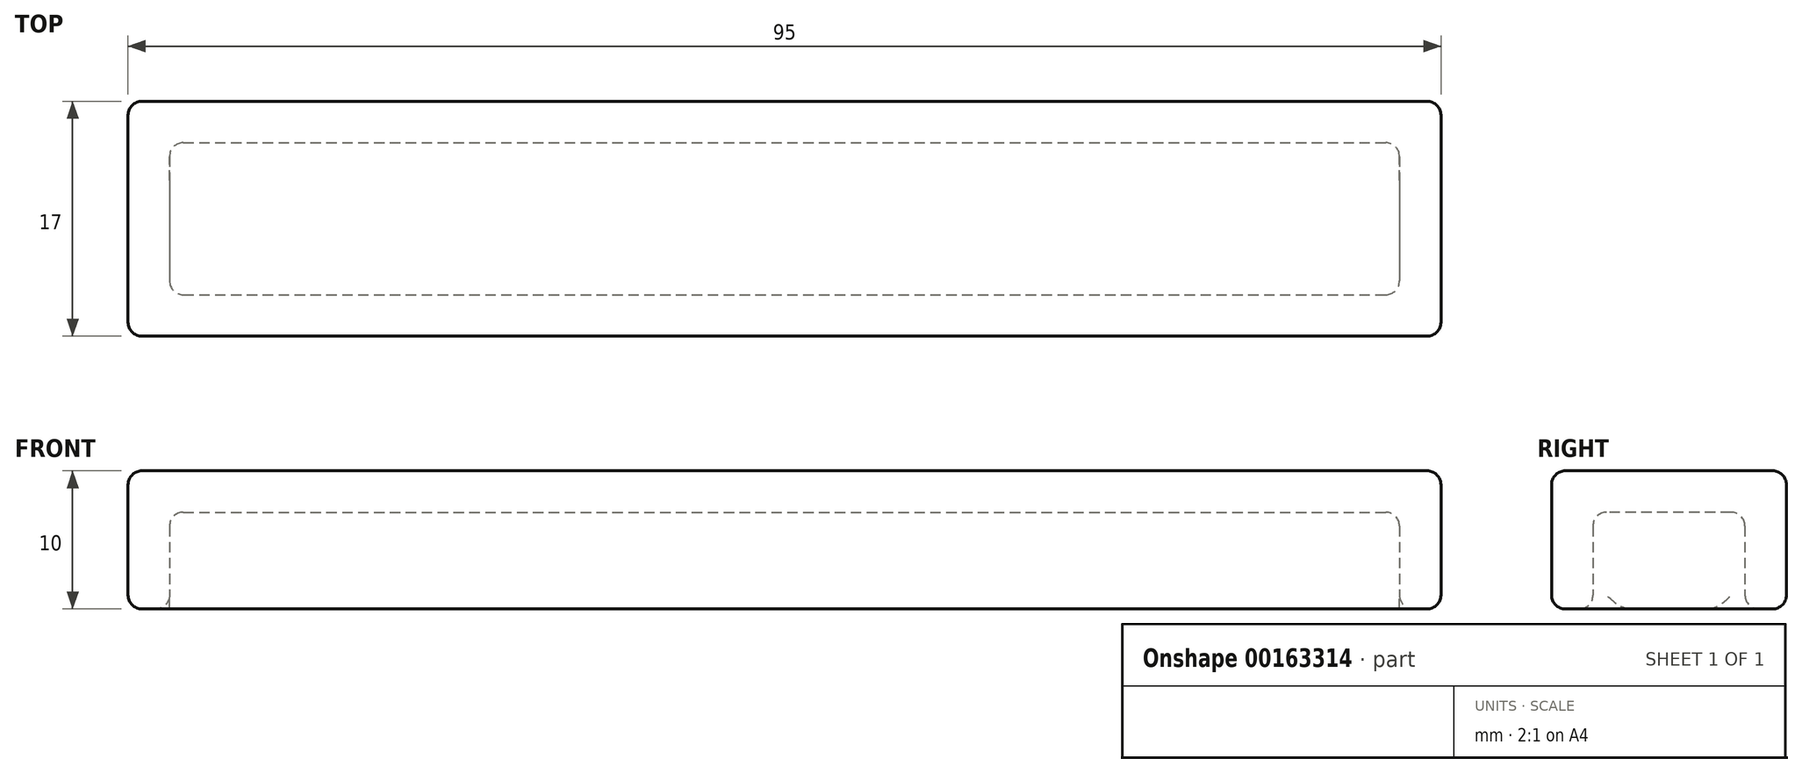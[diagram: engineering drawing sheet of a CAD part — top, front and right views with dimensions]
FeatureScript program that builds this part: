
annotation { "Feature Type Name" : "Feature", "Feature Type Description" : "" }
export const myFeature = defineFeature(function(context is Context, id is Id, definition is map)
    precondition{}
    {
        {
            var Q0;
            Q0=qCreatedBy(makeId("Top.planeOp"),FACE);
            var sketch = newSketch(context, id + "F0", { "sketchPlane" : qUnion([Q0])});
            skLineSegment(sketch, "E0.bottom", {"start": v(-44.64, 0) * mm, "end": v(44.36, 0) * mm, "construction": true});
            skLineSegment(sketch, "E0.top", {"start": v(-44.64, -11) * mm, "end": v(44.36, -11) * mm, "construction": true});
            skLineSegment(sketch, "E0.left", {"start": v(-44.64, 0) * mm, "end": v(-44.64, -11) * mm, "construction": true});
            skLineSegment(sketch, "E0.right", {"start": v(44.36, 0) * mm, "end": v(44.36, -11) * mm, "construction": true});
            skLineSegment(sketch, "E1.0", {"start": v(-47.64, 3) * mm, "end": v(-47.64, -14) * mm});
            skLineSegment(sketch, "E1.1", {"start": v(-47.64, 3) * mm, "end": v(47.36, 3) * mm});
            skLineSegment(sketch, "E1.2", {"start": v(47.36, 3) * mm, "end": v(47.36, -14) * mm});
            skLineSegment(sketch, "E1.3", {"start": v(-47.64, -14) * mm, "end": v(47.36, -14) * mm});
            skSolve(sketch);
        }
        {
            var Q0;
            Q0 = qSketchRegion(id + "F0", true);
            extrude(context, id + "F1", {"entities" : qUnion([Q0]), "depth" : 10 * mm});
        }
        {
            var Q0;
            Q0=makeQuery(id+"F1.opExtrude","CAP_FACE",FACE,{"disambiguationData":[OSD([sQuery(id+"F0.wireOp",EDGE,"E1.0"),sQuery(id+"F0.wireOp",EDGE,"E1.1"),sQuery(id+"F0.wireOp",EDGE,"E1.2"),sQuery(id+"F0.wireOp",EDGE,"E1.3")])],"isStart":true});
            shell(context, id + "F2", {"entities" : qUnion([Q0]), "thickness" : 3 * mm});
        }
        {
            var Q0;
            Q0=makeQuery(id+"F2.opShell","OFFSET_FACE",FACE,{"disambiguationData":[OSD([sQuery(id+"F0.wireOp",EDGE,"E1.0"),sQuery(id+"F0.wireOp",EDGE,"E1.1"),sQuery(id+"F0.wireOp",EDGE,"E1.2"),sQuery(id+"F0.wireOp",EDGE,"E1.3")])]});
            var Q1;
            Q1=makeQuery(id+"F2.opShell","OFFSET_FACE",FACE,{"disambiguationData":[OSD([sQuery(id+"F0.wireOp",EDGE,"E1.1")])]});
            var Q2;
            Q2=makeQuery(id+"F2.opShell","OFFSET_FACE",FACE,{"disambiguationData":[OSD([sQuery(id+"F0.wireOp",EDGE,"E1.3")])]});
            var Q3;
            Q3=makeQuery(id+"F1.opExtrude","SWEPT_FACE",FACE,{"disambiguationData":[OSD([sQuery(id+"F0.wireOp",EDGE,"E1.2")])]});
            var Q4;
            Q4=makeQuery(id+"F1.opExtrude","SWEPT_FACE",FACE,{"disambiguationData":[OSD([sQuery(id+"F0.wireOp",EDGE,"E1.3")])]});
            var Q5;
            Q5=makeQuery(id+"F1.opExtrude","SWEPT_FACE",FACE,{"disambiguationData":[OSD([sQuery(id+"F0.wireOp",EDGE,"E1.1")])]});
            var Q6;
            Q6=makeQuery(id+"F1.opExtrude","SWEPT_FACE",FACE,{"disambiguationData":[OSD([sQuery(id+"F0.wireOp",EDGE,"E1.0")])]});
            fillet(context, id + "F3", {"entities" : qUnion([Q0, Q1, Q2, Q3, Q4, Q5, Q6]), "radius" : 1 * mm, "tangentPropagation" : true, "allowEdgeOverflow" : false});
        }
    });
